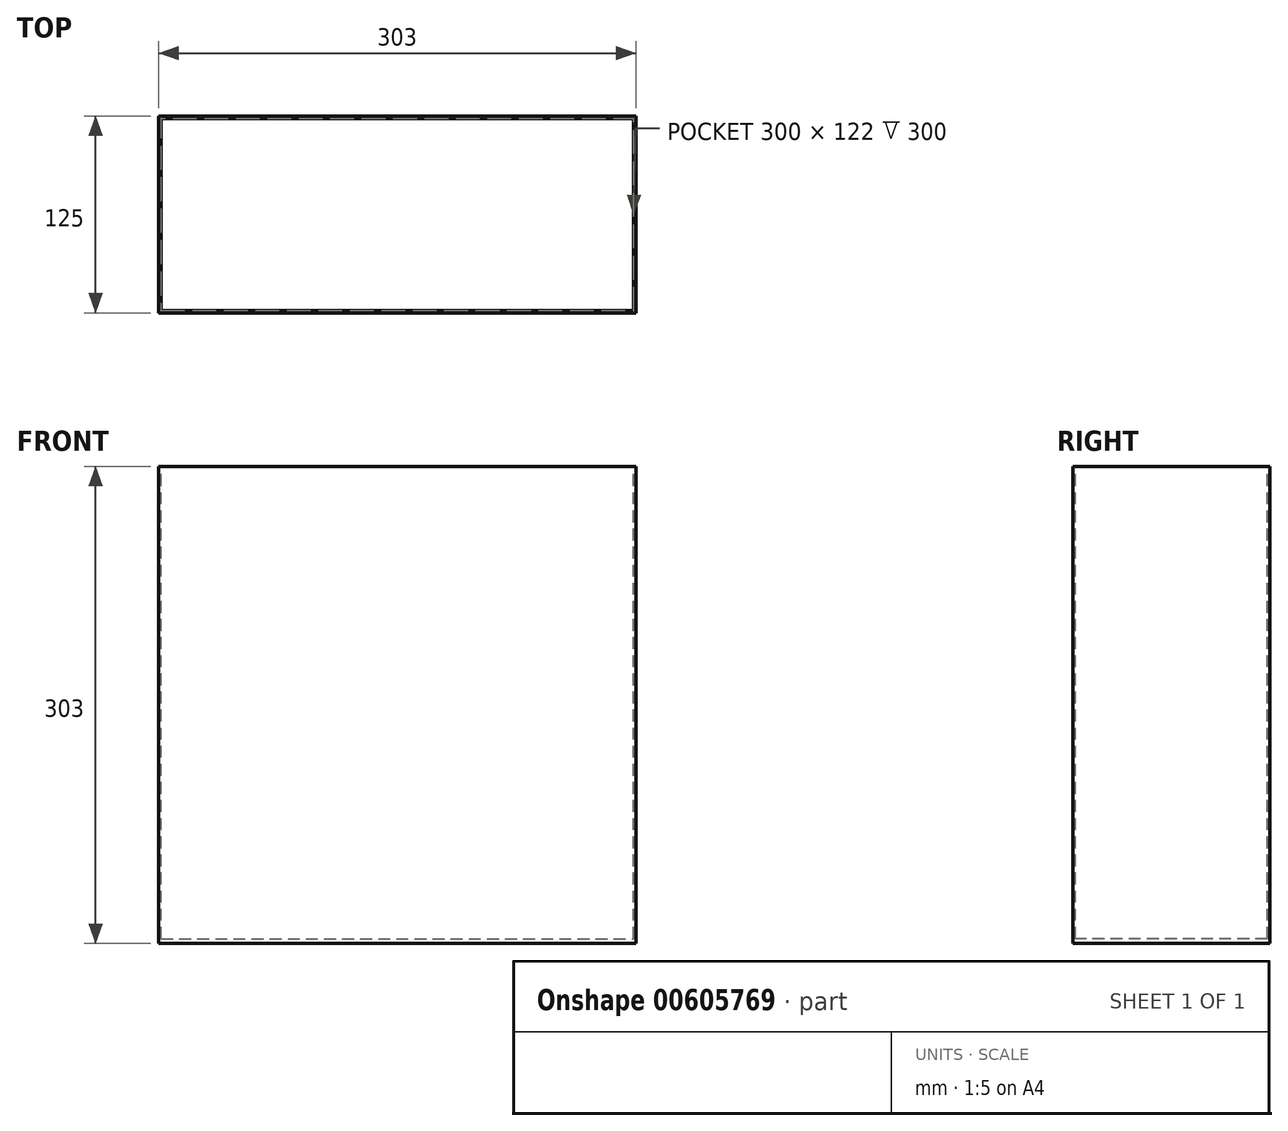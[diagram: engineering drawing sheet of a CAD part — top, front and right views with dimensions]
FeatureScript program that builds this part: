
annotation { "Feature Type Name" : "Feature", "Feature Type Description" : "" }
export const myFeature = defineFeature(function(context is Context, id is Id, definition is map)
    precondition{}
    {
        {
            var Q0;
            Q0=qCreatedBy(makeId("Front.planeOp"),FACE);
            var sketch = newSketch(context, id + "F0", { "sketchPlane" : qUnion([Q0])});
            skLineSegment(sketch, "E0.bottom", {"start": v(-151.5, 151.5) * mm, "end": v(151.5, 151.5) * mm});
            skLineSegment(sketch, "E0.top", {"start": v(-151.5, -151.5) * mm, "end": v(151.5, -151.5) * mm});
            skLineSegment(sketch, "E0.left", {"start": v(-151.5, 151.5) * mm, "end": v(-151.5, -151.5) * mm});
            skLineSegment(sketch, "E0.right", {"start": v(151.5, 151.5) * mm, "end": v(151.5, -151.5) * mm});
            skSolve(sketch);
        }
        {
            var Q0;
            Q0 = qSketchRegion(id + "F0", true);
            extrude(context, id + "F1", {"entities" : qUnion([Q0]), "depth" : 125 * mm, "offsetDistance" : 25 * mm});
        }
        {
            var Q0;
            Q0=makeQuery(id+"F1.opExtrude","SWEPT_FACE",FACE,{"disambiguationData":[OSD([sQuery(id+"F0.wireOp",EDGE,"E0.bottom")])]});
            var sketch = newSketch(context, id + "F2", { "sketchPlane" : qUnion([Q0])});
            skLineSegment(sketch, "E1.bottom", {"start": v(-150, -1.5) * mm, "end": v(150, -1.5) * mm});
            skLineSegment(sketch, "E1.top", {"start": v(-150, -123.5) * mm, "end": v(150, -123.5) * mm});
            skLineSegment(sketch, "E1.left", {"start": v(-150, -1.5) * mm, "end": v(-150, -123.5) * mm});
            skLineSegment(sketch, "E1.right", {"start": v(150, -1.5) * mm, "end": v(150, -123.5) * mm});
            skLineSegment(sketch, "E2", {"start": v(-12.97, -62.5) * mm, "end": v(12.79, -62.5) * mm, "construction": true});
            skLineSegment(sketch, "E3", {"start": v(0, 8.64) * mm, "end": v(0, -13.3) * mm, "construction": true});
            skSolve(sketch);
        }
        {
            var Q0;
            Q0 = qSketchRegion(id + "F2", true);
            extrude(context, id + "F3", {"entities" : qUnion([Q0]), "operationType" : NewBodyOperationType.REMOVE, "oppositeDirection" : true, "depth" : 300 * mm, "offsetDistance" : 25 * mm});
        }
    });
